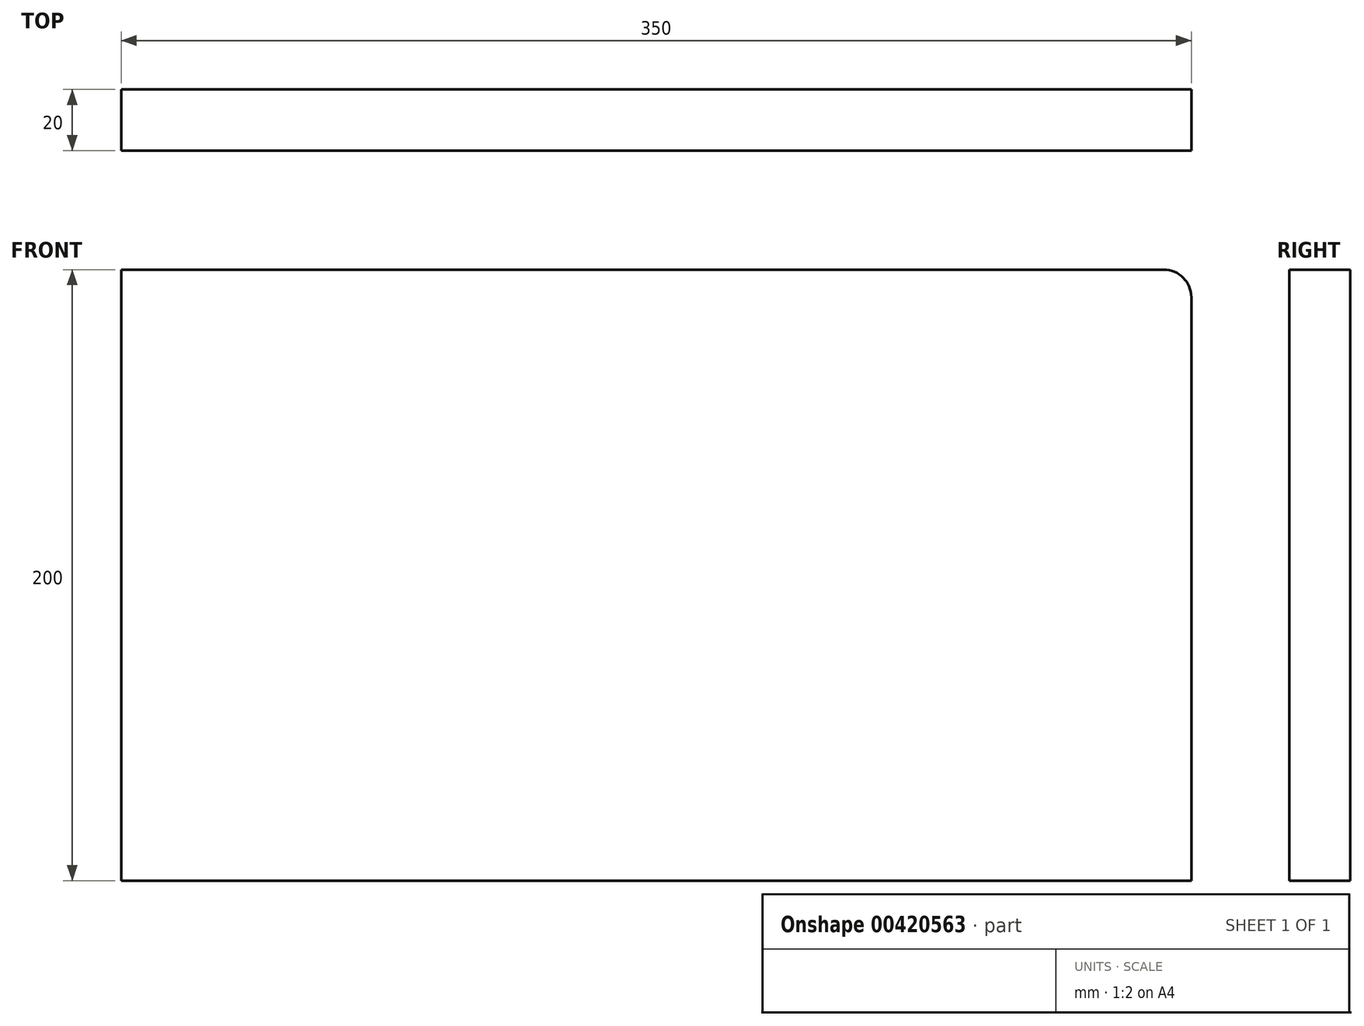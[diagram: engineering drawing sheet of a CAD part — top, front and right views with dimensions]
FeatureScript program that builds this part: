
annotation { "Feature Type Name" : "Feature", "Feature Type Description" : "" }
export const myFeature = defineFeature(function(context is Context, id is Id, definition is map)
    precondition{}
    {
        {
            var Q0;
            Q0=qCreatedBy(makeId("Front.planeOp"),FACE);
            var sketch = newSketch(context, id + "F0", { "sketchPlane" : qUnion([Q0])});
            skLineSegment(sketch, "E0.bottom", {"start": v(175, -100) * mm, "end": v(-175, -100) * mm});
            skLineSegment(sketch, "E0.top", {"start": v(175, 100) * mm, "end": v(-175, 100) * mm});
            skLineSegment(sketch, "E0.left", {"start": v(175, -100) * mm, "end": v(175, 100) * mm});
            skLineSegment(sketch, "E0.right", {"start": v(-175, -100) * mm, "end": v(-175, 100) * mm});
            skPoint(sketch, "E0.middle", {"position": v(0, 0) * mm});
            skSolve(sketch);
        }
        {
            var Q0;
            Q0 = qSketchRegion(id + "F0", true);
            extrude(context, id + "F1", {"entities" : qUnion([Q0]), "depth" : 20 * mm});
        }
        {
            var Q0;
            Q0=makeQuery(id+"F1.opExtrude","SWEPT_EDGE",EDGE,{"disambiguationData":[OSD([sQuery(id+"F0.wireOp",EDGE,"E0.top"),sQuery(id+"F0.wireOp",EDGE,"E0.left")])]});
            fillet(context, id + "F2", {"entities" : qUnion([Q0]), "radius" : 9 * mm, "tangentPropagation" : true, "allowEdgeOverflow" : false});
        }
    });
